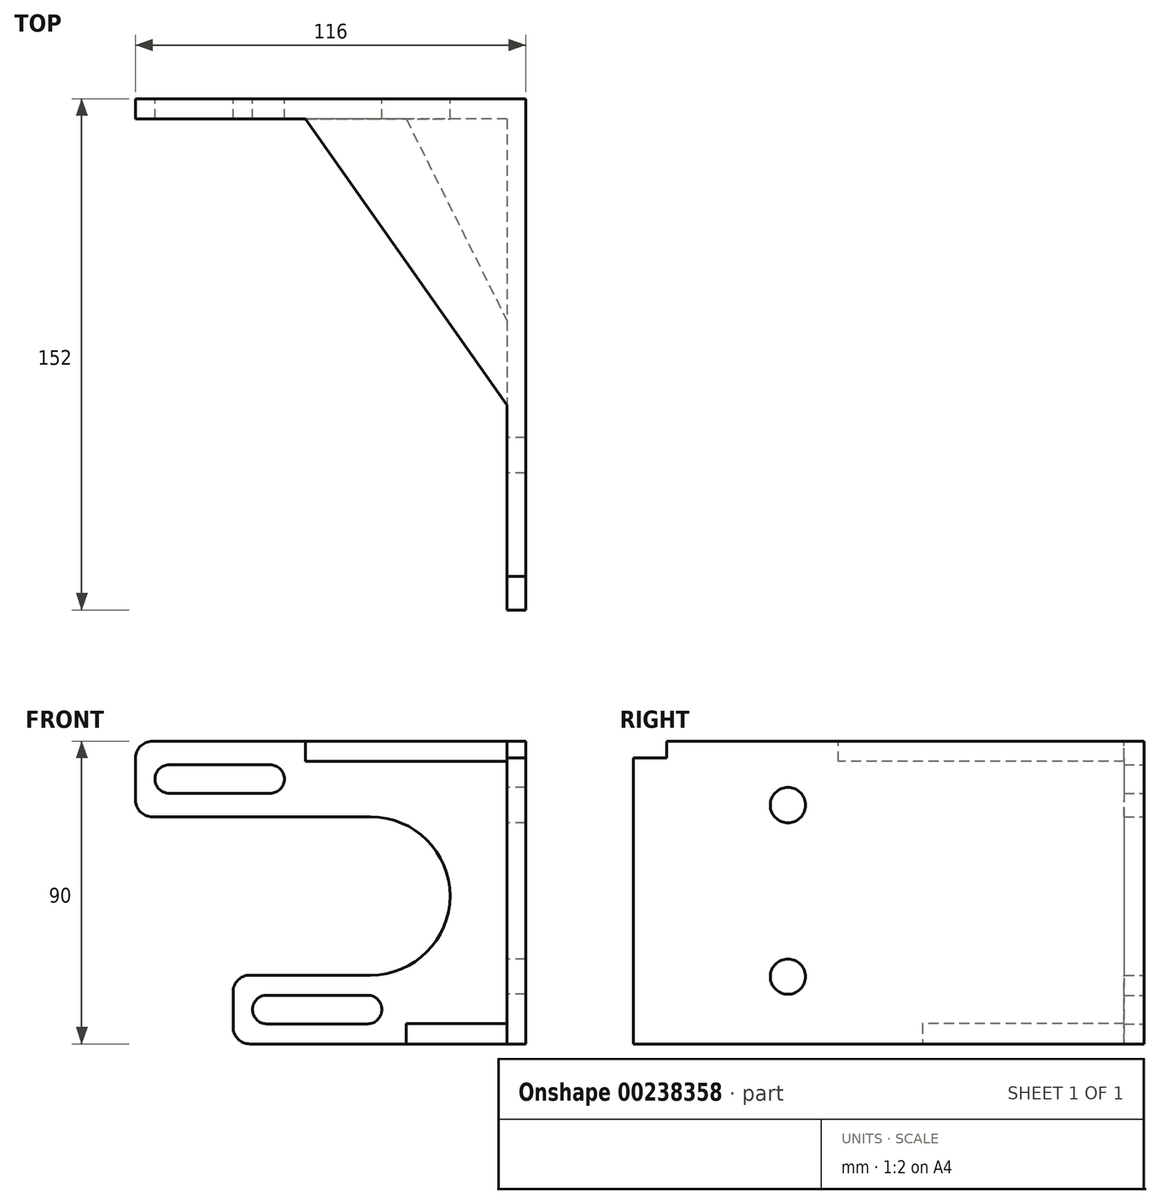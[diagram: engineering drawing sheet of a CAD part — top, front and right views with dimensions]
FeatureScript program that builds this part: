
annotation { "Feature Type Name" : "Feature", "Feature Type Description" : "" }
export const myFeature = defineFeature(function(context is Context, id is Id, definition is map)
    precondition{}
    {
        {
            var Q0;
            Q0=qCreatedBy(makeId("Right.planeOp"),FACE);
            var sketch = newSketch(context, id + "F0", { "sketchPlane" : qUnion([Q0])});
            skLineSegment(sketch, "E0.bottom", {"start": v(76, 45) * mm, "end": v(-66, 45) * mm});
            skLineSegment(sketch, "E0.top", {"start": v(76, -45) * mm, "end": v(-76, -45) * mm});
            skLineSegment(sketch, "E0.left", {"start": v(76, 45) * mm, "end": v(76, -45) * mm});
            skLineSegment(sketch, "E0.right", {"start": v(-76, 40) * mm, "end": v(-76, -45) * mm});
            skPoint(sketch, "E0.middle", {"position": v(0, 0) * mm});
            skCircle(sketch, "E1", {"center": v(-30, 26) * mm, "radius": 5.25 * mm});
            skCircle(sketch, "E2", {"center": v(-30, -25) * mm, "radius": 5.25 * mm});
            skLineSegment(sketch, "E3", {"start": v(-30, 26) * mm, "end": v(-30, -25) * mm, "construction": true});
            skLineSegment(sketch, "E4", {"start": v(-76, 40) * mm, "end": v(-66, 40) * mm});
            skLineSegment(sketch, "E5", {"start": v(-66, 40) * mm, "end": v(-66, 45) * mm});
            skPoint(sketch, "E6.orphan", {"position": v(-76, 45) * mm});
            skSolve(sketch);
        }
        {
            var Q0;
            Q0=qSketchRegion(id+"F0",true);
            extrude(context, id + "F1", {"entities" : qUnion([Q0]), "depth" : 5.5 * mm});
        }
        {
            var Q0;
            Q0=makeQuery(id+"F1.opExtrude","SWEPT_FACE",FACE,{"disambiguationData":[OSD([sQuery(id+"F0.wireOp",EDGE,"E0.left")])]});
            var sketch = newSketch(context, id + "F2", { "sketchPlane" : qUnion([Q0])});
            skLineSegment(sketch, "E7.0", {"start": v(0, 45) * mm, "end": v(0, -45) * mm});
            skLineSegment(sketch, "E8", {"start": v(0, 45) * mm, "end": v(110.5, 45) * mm});
            skLineSegment(sketch, "E9", {"start": v(110.5, 45) * mm, "end": v(110.5, 22.5) * mm});
            skLineSegment(sketch, "E10", {"start": v(110.5, 22.5) * mm, "end": v(40.53, 22.5) * mm});
            skLineSegment(sketch, "E11", {"start": v(0, -45) * mm, "end": v(81.5, -45) * mm});
            skLineSegment(sketch, "E12", {"start": v(81.5, -45) * mm, "end": v(81.5, -24.55) * mm});
            skLineSegment(sketch, "E13", {"start": v(81.5, -24.55) * mm, "end": v(40.52, -24.55) * mm});
            skLineSegment(sketch, "E14", {"start": v(17, 22.5) * mm, "end": v(17, -24.55) * mm, "construction": true});
            skArc(sketch, "E15", {"start": v(40.53, 22.5) * mm, "mid": v(17, -1.02) * mm, "end": v(40.53, -24.55) * mm});
            skLineSegment(sketch, "E16", {"start": v(110.5, 33.75) * mm, "end": v(70.5, 33.75) * mm, "construction": true});
            skLineSegment(sketch, "E17", {"start": v(81.5, -34.77) * mm, "end": v(41.5, -34.77) * mm, "construction": true});
            skArc(sketch, "E18", {"start": v(71.5, -39.02) * mm, "mid": v(75.75, -34.77) * mm, "end": v(71.5, -30.52) * mm});
            skArc(sketch, "E19", {"start": v(41.5, -30.52) * mm, "mid": v(37.25, -34.77) * mm, "end": v(41.5, -39.02) * mm});
            skArc(sketch, "E20", {"start": v(100.5, 29.5) * mm, "mid": v(104.75, 33.75) * mm, "end": v(100.5, 38) * mm});
            skArc(sketch, "E21", {"start": v(70.5, 38) * mm, "mid": v(66.25, 33.75) * mm, "end": v(70.5, 29.5) * mm});
            skLineSegment(sketch, "E22", {"start": v(70.5, 38) * mm, "end": v(100.5, 38) * mm});
            skLineSegment(sketch, "E23", {"start": v(70.5, 29.5) * mm, "end": v(100.5, 29.5) * mm});
            skLineSegment(sketch, "E24", {"start": v(41.5, -39.02) * mm, "end": v(71.5, -39.02) * mm});
            skLineSegment(sketch, "E25", {"start": v(41.5, -30.52) * mm, "end": v(71.5, -30.52) * mm});
            skSolve(sketch);
        }
        {
            var Q0;
            Q0 = qSketchRegion(id + "F2", true);
            extrude(context, id + "F3", {"entities" : qUnion([Q0]), "operationType" : NewBodyOperationType.ADD, "oppositeDirection" : true, "depth" : 6 * mm});
        }
        {
            var Q0;
            Q0=makeQuery(id+"F3.boolean.opBoolean","MERGE",FACE,{"derivedFrom":[makeQuery(id+"F1.opExtrude","SWEPT_FACE",FACE,{"disambiguationData":[OSD([sQuery(id+"F0.wireOp",EDGE,"E0.bottom")])]}),makeQuery(id+"F3.opExtrude","SWEPT_FACE",FACE,{"disambiguationData":[OSD([sQuery(id+"F2.wireOp",EDGE,"E8")])]})]});
            var sketch = newSketch(context, id + "F4", { "sketchPlane" : qUnion([Q0])});
            skLineSegment(sketch, "E26.0", {"start": v(0, 70) * mm, "end": v(-60, 70) * mm});
            skLineSegment(sketch, "E26.1", {"start": v(0, 70) * mm, "end": v(0, -15) * mm});
            skLineSegment(sketch, "E27", {"start": v(-60, 70) * mm, "end": v(0, -15) * mm});
            skPoint(sketch, "E28.orphan", {"position": v(-110.5, 70) * mm});
            skPoint(sketch, "E29.orphan", {"position": v(0, -66) * mm});
            skSolve(sketch);
        }
        {
            var Q0;
            Q0 = qSketchRegion(id + "F4", true);
            extrude(context, id + "F5", {"entities" : qUnion([Q0]), "operationType" : NewBodyOperationType.ADD, "oppositeDirection" : true, "depth" : 6 * mm});
        }
        {
            var Q0;
            Q0=makeQuery(id+"F3.boolean.opBoolean","MERGE",FACE,{"derivedFrom":[makeQuery(id+"F1.opExtrude","SWEPT_FACE",FACE,{"disambiguationData":[OSD([sQuery(id+"F0.wireOp",EDGE,"E0.top")])]}),makeQuery(id+"F3.opExtrude","SWEPT_FACE",FACE,{"disambiguationData":[OSD([sQuery(id+"F2.wireOp",EDGE,"E11")])]})]});
            var sketch = newSketch(context, id + "F6", { "sketchPlane" : qUnion([Q0])});
            skLineSegment(sketch, "E30.0", {"start": v(0, -70) * mm, "end": v(0, -10) * mm});
            skLineSegment(sketch, "E30.1", {"start": v(0, -70) * mm, "end": v(-30, -70) * mm});
            skLineSegment(sketch, "E31", {"start": v(-30, -70) * mm, "end": v(0, -10) * mm});
            skPoint(sketch, "E32.orphan", {"position": v(-81.5, -70) * mm});
            skPoint(sketch, "E33.orphan", {"position": v(0, 76) * mm});
            skSolve(sketch);
        }
        {
            var Q0;
            Q0 = qSketchRegion(id + "F6", true);
            extrude(context, id + "F7", {"entities" : qUnion([Q0]), "operationType" : NewBodyOperationType.ADD, "oppositeDirection" : true, "depth" : 6 * mm});
        }
        {
            var Q0;
            Q0=makeQuery(id+"F3.opExtrude","SWEPT_EDGE",EDGE,{"disambiguationData":[OSD([sQuery(id+"F2.wireOp",EDGE,"E8"),sQuery(id+"F2.wireOp",EDGE,"E9")])]});
            var Q1;
            Q1=makeQuery(id+"F3.opExtrude","SWEPT_EDGE",EDGE,{"disambiguationData":[OSD([sQuery(id+"F2.wireOp",EDGE,"E9"),sQuery(id+"F2.wireOp",EDGE,"E10")])]});
            var Q2;
            Q2=makeQuery(id+"F3.opExtrude","SWEPT_EDGE",EDGE,{"disambiguationData":[OSD([sQuery(id+"F2.wireOp",EDGE,"E12"),sQuery(id+"F2.wireOp",EDGE,"E13")])]});
            var Q3;
            Q3=makeQuery(id+"F3.opExtrude","SWEPT_EDGE",EDGE,{"disambiguationData":[OSD([sQuery(id+"F2.wireOp",EDGE,"E11"),sQuery(id+"F2.wireOp",EDGE,"E12")])]});
            fillet(context, id + "F8", {"entities" : qUnion([Q0, Q1, Q2, Q3]), "radius" : 5 * mm, "tangentPropagation" : true, "allowEdgeOverflow" : false});
        }
    });
